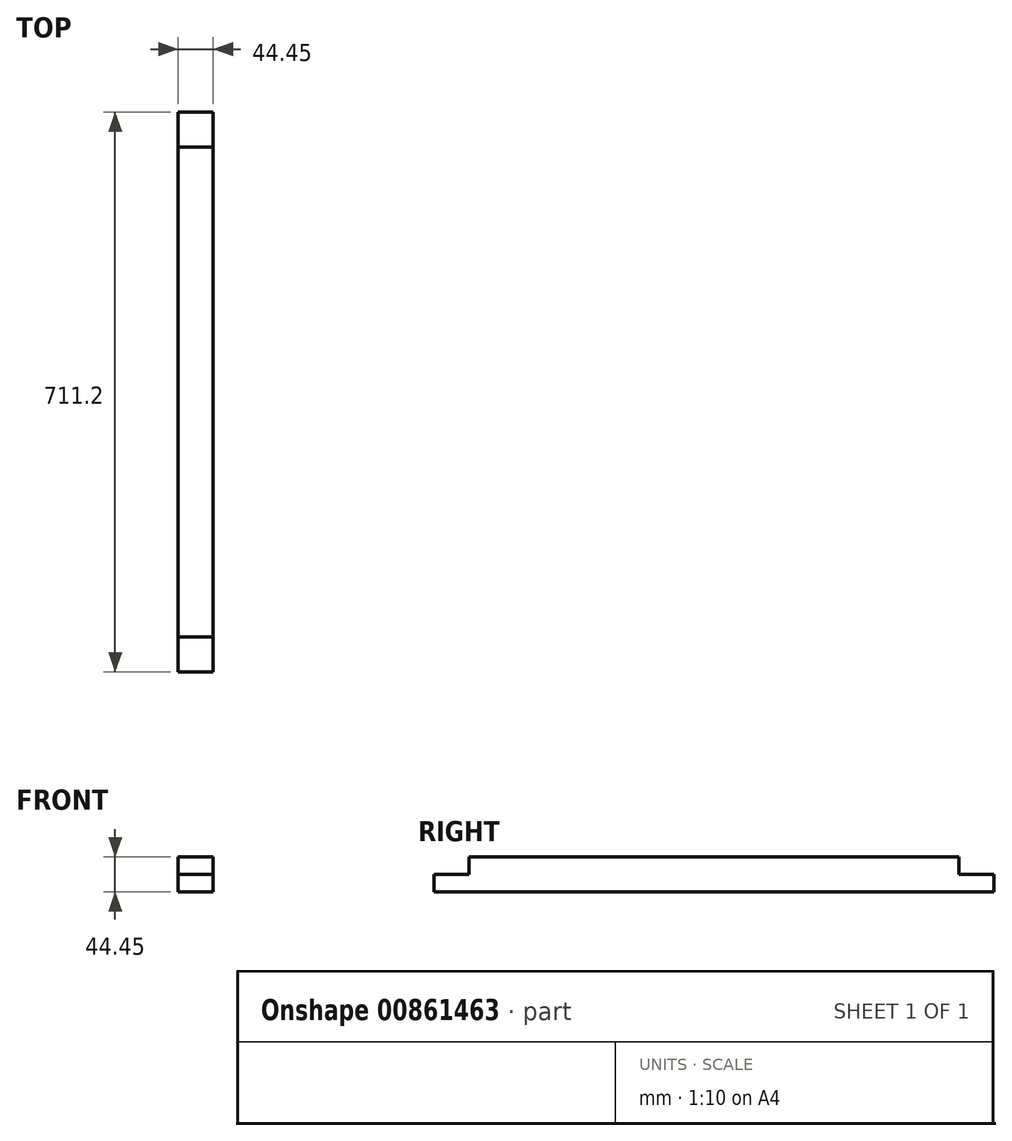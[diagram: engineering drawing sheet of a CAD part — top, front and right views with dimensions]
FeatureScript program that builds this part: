
annotation { "Feature Type Name" : "Feature", "Feature Type Description" : "" }
export const myFeature = defineFeature(function(context is Context, id is Id, definition is map)
    precondition{}
    {
        {
            var Q0;
            Q0=qCreatedBy(makeId("Front.planeOp"),FACE);
            var sketch = newSketch(context, id + "F0", { "sketchPlane" : qUnion([Q0])});
            skLineSegment(sketch, "E0.bottom", {"start": v(0, 0) * mm, "end": v(44.45, 0) * mm});
            skLineSegment(sketch, "E0.top", {"start": v(0, 44.45) * mm, "end": v(44.45, 44.45) * mm});
            skLineSegment(sketch, "E0.left", {"start": v(0, 0) * mm, "end": v(0, 44.45) * mm});
            skLineSegment(sketch, "E0.right", {"start": v(44.45, 0) * mm, "end": v(44.45, 44.45) * mm});
            skSolve(sketch);
        }
        {
            var Q0;
            Q0=makeQuery(id+"F0.imprint","IMPRINT",FACE,{"disambiguationData":[TD([[makeQuery(id+"F0.imprint","IMPRINT",EDGE,{"derivedFrom":sQuery(id+"F0.wireOp",EDGE,"E0.bottom")}),1.0]])]});
            extrude(context, id + "F1", {"entities" : qUnion([Q0]), "depth" : 711.2 * mm, "offsetDistance" : 25.4 * mm});
        }
        {
            var Q0;
            Q0=makeQuery(id+"F1.opExtrude","SWEPT_FACE",FACE,{"disambiguationData":[OSD([sQuery(id+"F0.wireOp",EDGE,"E0.top")])]});
            var sketch = newSketch(context, id + "F2", { "sketchPlane" : qUnion([Q0])});
            skLineSegment(sketch, "E1.bottom", {"start": v(0, -711.2) * mm, "end": v(44.45, -711.2) * mm});
            skLineSegment(sketch, "E1.top", {"start": v(0, -666.75) * mm, "end": v(44.45, -666.75) * mm});
            skLineSegment(sketch, "E1.left", {"start": v(0, -711.2) * mm, "end": v(0, -666.75) * mm});
            skLineSegment(sketch, "E1.right", {"start": v(44.45, -711.2) * mm, "end": v(44.45, -666.75) * mm});
            skLineSegment(sketch, "E2.bottom", {"start": v(0, 0) * mm, "end": v(44.45, 0) * mm});
            skLineSegment(sketch, "E2.top", {"start": v(0, -44.45) * mm, "end": v(44.45, -44.45) * mm});
            skLineSegment(sketch, "E2.left", {"start": v(0, 0) * mm, "end": v(0, -44.45) * mm});
            skLineSegment(sketch, "E2.right", {"start": v(44.45, 0) * mm, "end": v(44.45, -44.45) * mm});
            skSolve(sketch);
        }
        {
            var Q0;
            Q0 = qSketchRegion(id + "F2", true);
            extrude(context, id + "F3", {"entities" : qUnion([Q0]), "operationType" : NewBodyOperationType.REMOVE, "oppositeDirection" : true, "depth" : 22.22 * mm, "offsetDistance" : 25.4 * mm});
        }
    });
